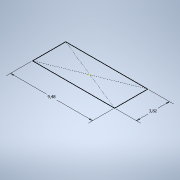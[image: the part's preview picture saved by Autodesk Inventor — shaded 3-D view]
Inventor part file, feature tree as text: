
AUTODESK INVENTOR PART (.ipt)
format: ipt  version: 2022 (Build 260153000, 153)  size: 94,720 bytes
history: native  units: mm
features: other x1, extrude x1, sketch x1
ambient origin geometry x8: Origin, YZ Plane, XZ Plane, XY Plane, X Axis, Y Axis, Z Axis, Center Point
bodies: Body1 (feature_tree)
feature tree (3):
  other  "Твердое тело1"
  extrude  "Выдавливание1"  Depth=9.48mm
  sketch  "Эскиз1"
